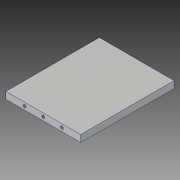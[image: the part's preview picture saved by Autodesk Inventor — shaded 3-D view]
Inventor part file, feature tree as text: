
AUTODESK INVENTOR PART (.ipt)
format: ipt  version: 2019 (Build 230136000, 136)  size: 100,352 bytes
history: native  units: mm
features: sketch x3, hole x2, extrude x1
ambient origin geometry x8: Origin, YZ Plane, XZ Plane, XY Plane, X Axis, Y Axis, Z Axis, Center Point
bodies: Solid1 (feature_tree)
feature tree (6):
  extrude  "Extrusion1"  Depth=135.0mm
  hole  "Hole1"  [1 undecoded]
  hole  "Hole2"  [1 undecoded]
  sketch  "Sketch1"  dims[d0=108.0mm d1=135.0mm]
  sketch  "Sketch2"  dims[d2=10.0mm d3=0.0mm d4=54.0mm]
  sketch  "Sketch3"  dims[d5=4.134mm d6=10.0mm d7=4.0mm d8=2.0mm d9=90.0deg d10=14.2mm d11=20.594885mm d12=4.134mm d13=10.0mm d14=4.0mm d15=2.0mm d16=90.0deg d17=14.2mm d18=20.594885mm]
note: 2 required parameter values undecoded (feature->parameter linkage not recoverable at this tier; creation-order binding heuristic only, values carry confidence <= 0.55)
